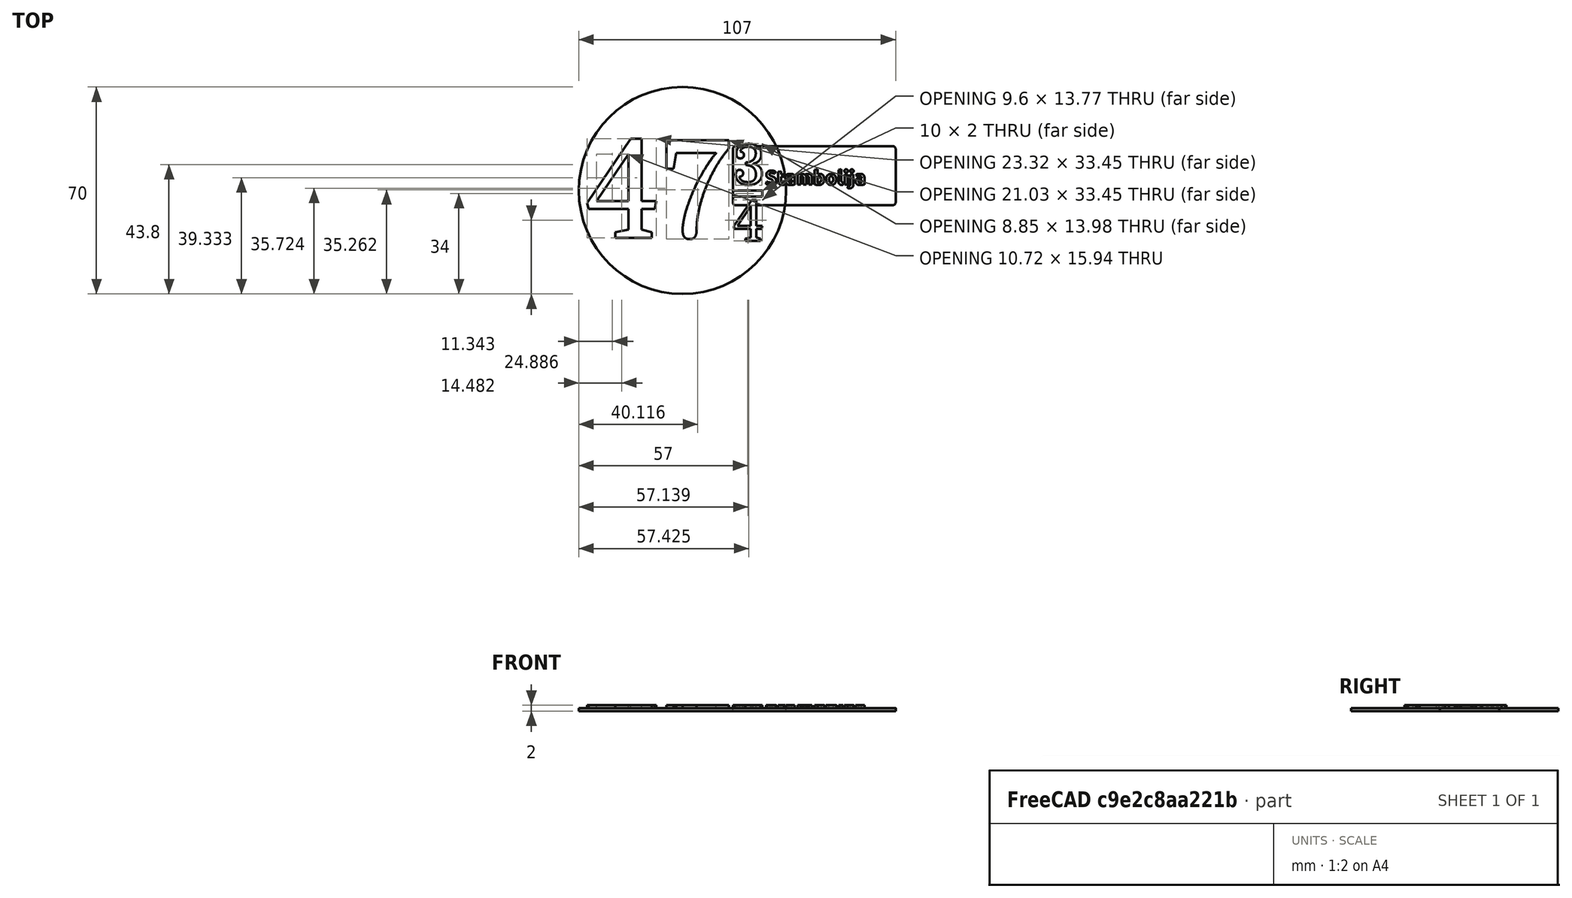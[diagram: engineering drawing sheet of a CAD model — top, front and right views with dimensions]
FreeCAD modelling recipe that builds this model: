
FCSTD DOCUMENT  (FreeCAD 0.20R29177 +426 (Git))
Label: Plocica_postansko_sanduce
License: All rights reserved
LicenseURL: http://en.wikipedia.org/wiki/All_rights_reserved
objects: Part::Part2DObjectPython×4, Part::Extrusion×4, Part::Box×2, Part::MultiFuse×2, Part::Fillet×1, Part::Cylinder×1
note: 14 computed .brp shape members not serialized (recipe doc carries the construction recipe); baked Part::Feature solids carry a one-line shape summary decoded from their .brp

FEATURE [Part::Box] Box  label="Cube"
  AttacherType = Attacher::AttachEngine3D
  Height = 1
  Length = 55
  Width = 20
FEATURE [Part::Part2DObjectPython] ShapeString001  label="PP"  # Draft 2D object (typed FeaturePython)
  FontFile = <userpath>/Projects/3D-Print-models/Ubuntu-B.ttf
  Placement = pos=(11,7,0) rot=(0,0,1;0rad)
  Size = 2.5
  String = Stambolija
  Tracking = 0
FEATURE [Part::Extrusion] Extrude001  label="PPEx"
  Base = -> ShapeString001
  Dir = (0,0,1)
  DirMode = 2
  FaceMakerClass = Part::FaceMakerBullseye
  LengthFwd = 2
  LengthRev = 0
  Solid = false
  Symmetric = false
FEATURE [Part::Fillet] Fillet
  Base = -> Box
  Edges = 4 edges r=1: [Edge1,Edge3,Edge5,Edge7]
FEATURE [Part::MultiFuse] Fusion  label="Polocica_za_ptt"
  Shapes = -> [Extrude001,Fillet]
FEATURE [Part::Part2DObjectPython] ShapeString002  label="PP001"  # Draft 2D object (typed FeaturePython)
  FontFile = <userpath>/Projects/3D-Print-models/Domine-VariableFont_wght.ttf
  Size = 17
  String = 47
  Tracking = 0
FEATURE [Part::Extrusion] Extrude002  label="PPEx001"
  Base = -> ShapeString002
  Dir = (0,0,1)
  DirMode = 2
  FaceMakerClass = Part::FaceMakerBullseye
  LengthFwd = 2
  LengthRev = 0
  Placement = pos=(-50,-11,0) rot=(0,0,1;0rad)
  Solid = false
  Symmetric = false
FEATURE [Part::Part2DObjectPython] ShapeString003  label="PP002"  # Draft 2D object (typed FeaturePython)
  FontFile = <userpath>/Projects/3D-Print-models/Domine-VariableFont_wght.ttf
  Size = 7
  String = 3
  Tracking = 0
FEATURE [Part::Extrusion] Extrude003  label="PPEx002"
  Base = -> ShapeString003
  Dir = (0,0,1)
  DirMode = 2
  FaceMakerClass = Part::FaceMakerBullseye
  LengthFwd = 2
  LengthRev = 0
  Placement = pos=(0,7,0) rot=(0,0,1;0rad)
  Solid = false
  Symmetric = false
FEATURE [Part::Box] Box001  label="Cube001"
  AttacherType = Attacher::AttachEngine3D
  Height = 2
  Length = 10
  Placement = pos=(0,3,0) rot=(0,0,1;0rad)
  Width = 2
FEATURE [Part::Part2DObjectPython] ShapeString004  label="PP003"  # Draft 2D object (typed FeaturePython)
  FontFile = <userpath>/Projects/3D-Print-models/Domine-VariableFont_wght.ttf
  Size = 7
  String = 4
  Tracking = 0
FEATURE [Part::Extrusion] Extrude004  label="PPEx003"
  Base = -> ShapeString004
  Dir = (0,0,1)
  DirMode = 2
  FaceMakerClass = Part::FaceMakerBullseye
  LengthFwd = 2
  LengthRev = 0
  Placement = pos=(0,-12,0) rot=(0,0,1;0rad)
  Solid = false
  Symmetric = false
FEATURE [Part::Cylinder] Cylinder
  Angle = 360
  AttacherType = Attacher::AttachEngine3D
  FirstAngle = 0
  Height = 1
  Placement = pos=(-17,5,0) rot=(0,0,1;0rad)
  Radius = 35
  SecondAngle = 0
FEATURE [Part::MultiFuse] Fusion001  label="Kanc"
  Shapes = -> [Extrude002,Extrude003,Box001,Extrude004,Cylinder]
